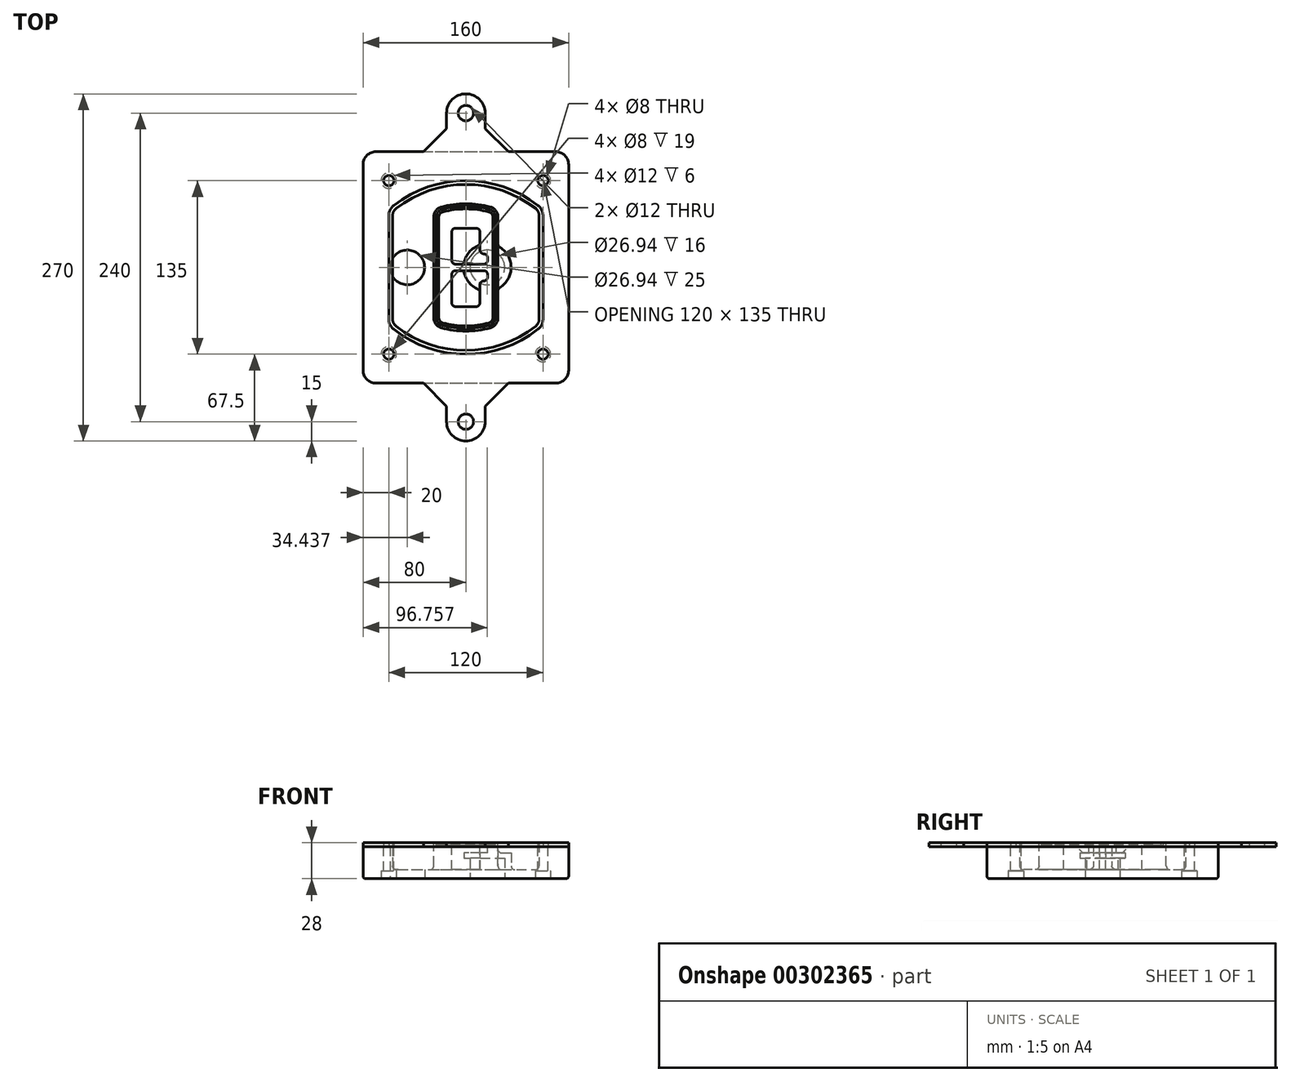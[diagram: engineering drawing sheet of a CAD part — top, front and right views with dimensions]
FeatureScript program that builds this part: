
annotation { "Feature Type Name" : "Feature", "Feature Type Description" : "" }
export const myFeature = defineFeature(function(context is Context, id is Id, definition is map)
    precondition{}
    {
        {
            var Q0;
            Q0=qCreatedBy(makeId("Top.planeOp"),FACE);
            var sketch = newSketch(context, id + "F0", { "sketchPlane" : qUnion([Q0])});
            skPoint(sketch, "E0.rect.middle", {"position": v(0, 0) * mm});
            skLineSegment(sketch, "E1.bottom", {"start": v(-70, -90) * mm, "end": v(70, -90) * mm});
            skLineSegment(sketch, "E1.top", {"start": v(-70, 90) * mm, "end": v(70, 90) * mm});
            skLineSegment(sketch, "E1.left", {"start": v(-80, -80) * mm, "end": v(-80, 80) * mm});
            skLineSegment(sketch, "E1.right", {"start": v(80, -80) * mm, "end": v(80, 80) * mm});
            skLineSegment(sketch, "E2", {"start": v(-80, 90) * mm, "end": v(80, -90) * mm, "construction": true});
            skLineSegment(sketch, "E3", {"start": v(80, 90) * mm, "end": v(-80, -90) * mm, "construction": true});
            skCircle(sketch, "E4", {"center": v(-60, 67.5) * mm, "radius": 4 * mm});
            skCircle(sketch, "E5", {"center": v(60, 67.5) * mm, "radius": 4 * mm});
            skCircle(sketch, "E6", {"center": v(60, -67.5) * mm, "radius": 4 * mm});
            skCircle(sketch, "E7", {"center": v(-60, -67.5) * mm, "radius": 4 * mm});
            skLineSegment(sketch, "E8", {"start": v(-60, 67.5) * mm, "end": v(60, 67.5) * mm, "construction": true});
            skLineSegment(sketch, "E9", {"start": v(60, 67.5) * mm, "end": v(60, -67.5) * mm, "construction": true});
            skLineSegment(sketch, "E10", {"start": v(60, -67.5) * mm, "end": v(-60, -67.5) * mm, "construction": true});
            skLineSegment(sketch, "E11", {"start": v(-60, -67.5) * mm, "end": v(-60, 67.5) * mm, "construction": true});
            skLineSegment(sketch, "E12", {"start": v(-60, 40.3) * mm, "end": v(-60, -40.3) * mm});
            skLineSegment(sketch, "E13", {"start": v(60, 40.3) * mm, "end": v(60, -40.3) * mm});
            skArc(sketch, "E14", {"start": v(56.15, 48.18) * mm, "mid": v(0, 67.5) * mm, "end": v(-56.15, 48.18) * mm});
            skArc(sketch, "E15", {"start": v(-56.15, -48.18) * mm, "mid": v(0, -67.5) * mm, "end": v(56.15, -48.18) * mm});
            skLineSegment(sketch, "E16", {"start": v(-60, 0) * mm, "end": v(60, 0) * mm, "construction": true});
            skPoint(sketch, "E17.visualSharp", {"position": v(-60, -45) * mm});
            skArc(sketch, "E17.filletArc", {"start": v(-60, -40.3) * mm, "mid": v(-58.99, -44.68) * mm, "end": v(-56.15, -48.18) * mm});
            skPoint(sketch, "E18.visualSharp", {"position": v(-60, 45) * mm});
            skArc(sketch, "E18.filletArc", {"start": v(-56.15, 48.18) * mm, "mid": v(-58.99, 44.68) * mm, "end": v(-60, 40.3) * mm});
            skPoint(sketch, "E19.visualSharp", {"position": v(60, 45) * mm});
            skArc(sketch, "E19.filletArc", {"start": v(60, 40.3) * mm, "mid": v(58.99, 44.68) * mm, "end": v(56.15, 48.18) * mm});
            skPoint(sketch, "E20.visualSharp", {"position": v(60, -45) * mm});
            skArc(sketch, "E20.filletArc", {"start": v(56.15, -48.18) * mm, "mid": v(58.99, -44.68) * mm, "end": v(60, -40.3) * mm});
            skPoint(sketch, "E21.visualSharp", {"position": v(-80, 90) * mm});
            skArc(sketch, "E21.filletArc", {"start": v(-70, 90) * mm, "mid": v(-77.07, 87.07) * mm, "end": v(-80, 80) * mm});
            skPoint(sketch, "E22.visualSharp", {"position": v(80, 90) * mm});
            skArc(sketch, "E22.filletArc", {"start": v(80, 80) * mm, "mid": v(77.07, 87.07) * mm, "end": v(70, 90) * mm});
            skPoint(sketch, "E23.visualSharp", {"position": v(80, -90) * mm});
            skArc(sketch, "E23.filletArc", {"start": v(70, -90) * mm, "mid": v(77.07, -87.07) * mm, "end": v(80, -80) * mm});
            skPoint(sketch, "E24.visualSharp", {"position": v(-80, -90) * mm});
            skArc(sketch, "E24.filletArc", {"start": v(-80, -80) * mm, "mid": v(-77.07, -87.07) * mm, "end": v(-70, -90) * mm});
            skArc(sketch, "E25.0", {"start": v(57, 40.3) * mm, "mid": v(56.3, 43.36) * mm, "end": v(54.3, 45.81) * mm});
            skLineSegment(sketch, "E25.1", {"start": v(57, 40.3) * mm, "end": v(57, -40.3) * mm});
            skArc(sketch, "E25.2", {"start": v(54.3, -45.81) * mm, "mid": v(56.3, -43.36) * mm, "end": v(57, -40.3) * mm});
            skArc(sketch, "E25.3", {"start": v(-54.3, -45.81) * mm, "mid": v(0, -64.5) * mm, "end": v(54.3, -45.81) * mm});
            skArc(sketch, "E25.4", {"start": v(-57, -40.3) * mm, "mid": v(-56.3, -43.36) * mm, "end": v(-54.3, -45.81) * mm});
            skArc(sketch, "E25.5", {"start": v(54.3, 45.81) * mm, "mid": v(0, 64.5) * mm, "end": v(-54.3, 45.81) * mm});
            skLineSegment(sketch, "E25.6", {"start": v(-57, 40.3) * mm, "end": v(-57, -40.3) * mm});
            skArc(sketch, "E25.7", {"start": v(-54.3, 45.81) * mm, "mid": v(-56.3, 43.36) * mm, "end": v(-57, 40.3) * mm});
            skArc(sketch, "E26.0", {"start": v(-58.62, 51.33) * mm, "mid": v(-62.58, 46.43) * mm, "end": v(-64, 40.3) * mm});
            skArc(sketch, "E26.1", {"start": v(58.62, 51.33) * mm, "mid": v(0, 71.5) * mm, "end": v(-58.62, 51.33) * mm});
            skArc(sketch, "E26.2", {"start": v(64, 40.3) * mm, "mid": v(62.58, 46.43) * mm, "end": v(58.62, 51.33) * mm});
            skLineSegment(sketch, "E26.3", {"start": v(64, 40.3) * mm, "end": v(64, -40.3) * mm});
            skArc(sketch, "E26.4", {"start": v(58.62, -51.33) * mm, "mid": v(62.58, -46.43) * mm, "end": v(64, -40.3) * mm});
            skLineSegment(sketch, "E26.5", {"start": v(-64, 40.3) * mm, "end": v(-64, -40.3) * mm});
            skArc(sketch, "E26.6", {"start": v(-58.62, -51.33) * mm, "mid": v(0, -71.5) * mm, "end": v(58.62, -51.33) * mm});
            skArc(sketch, "E26.7", {"start": v(-64, -40.3) * mm, "mid": v(-62.58, -46.43) * mm, "end": v(-58.62, -51.33) * mm});
            skSolve(sketch);
        }
        {
            var Q0;
            Q0=makeQuery(id+"F0.imprint","IMPRINT",FACE,{"disambiguationData":[TD([[makeQuery(id+"F0.imprint","IMPRINT",EDGE,{"derivedFrom":sQuery(id+"F0.wireOp",EDGE,"E1.bottom")}),1.0]])]});
            var Q1;
            Q1=makeQuery(id+"F0.imprint","IMPRINT",FACE,{"disambiguationData":[TD([[makeQuery(id+"F0.imprint","IMPRINT",EDGE,{"derivedFrom":sQuery(id+"F0.wireOp",EDGE,"E12")}),1.0]])]});
            var Q2;
            Q2=makeQuery(id+"F0.imprint","IMPRINT",FACE,{"disambiguationData":[TD([[makeQuery(id+"F0.imprint","IMPRINT",EDGE,{"derivedFrom":sQuery(id+"F0.wireOp",EDGE,"E25.0")}),1.0]])]});
            var Q3;
            Q3=makeQuery(id+"F0.imprint","IMPRINT",FACE,{"disambiguationData":[TD([[makeQuery(id+"F0.imprint","IMPRINT",EDGE,{"derivedFrom":sQuery(id+"F0.wireOp",EDGE,"E12")}),-1.0]])]});
            extrude(context, id + "F1", {"entities" : qUnion([Q0, Q1, Q2, Q3]), "oppositeDirection" : true, "depth" : 25 * mm});
        }
        {
            var Q0;
            Q0=makeQuery(id+"F0.imprint","IMPRINT",FACE,{"disambiguationData":[TD([[makeQuery(id+"F0.imprint","IMPRINT",EDGE,{"derivedFrom":sQuery(id+"F0.wireOp",EDGE,"E12")}),1.0]])]});
            extrude(context, id + "F2", {"entities" : qUnion([Q0]), "operationType" : NewBodyOperationType.ADD, "depth" : 3 * mm});
        }
        {
            var Q0;
            Q0=makeQuery(id+"F0.imprint","IMPRINT",FACE,{"disambiguationData":[TD([[makeQuery(id+"F0.imprint","IMPRINT",EDGE,{"derivedFrom":sQuery(id+"F0.wireOp",EDGE,"E25.0")}),1.0]])]});
            extrude(context, id + "F3", {"entities" : qUnion([Q0]), "operationType" : NewBodyOperationType.REMOVE, "oppositeDirection" : true, "depth" : 18 * mm});
        }
        {
            var Q0;
            Q0=makeQuery(id+"F2.opExtrude","CAP_FACE",FACE,{"disambiguationData":[OSD([sQuery(id+"F0.wireOp",EDGE,"E12"),sQuery(id+"F0.wireOp",EDGE,"E13"),sQuery(id+"F0.wireOp",EDGE,"E14"),sQuery(id+"F0.wireOp",EDGE,"E15"),sQuery(id+"F0.wireOp",EDGE,"E17.filletArc"),sQuery(id+"F0.wireOp",EDGE,"E18.filletArc"),sQuery(id+"F0.wireOp",EDGE,"E19.filletArc"),sQuery(id+"F0.wireOp",EDGE,"E20.filletArc"),sQuery(id+"F0.wireOp",EDGE,"E25.0"),sQuery(id+"F0.wireOp",EDGE,"E25.1"),sQuery(id+"F0.wireOp",EDGE,"E25.2"),sQuery(id+"F0.wireOp",EDGE,"E25.3"),sQuery(id+"F0.wireOp",EDGE,"E25.4"),sQuery(id+"F0.wireOp",EDGE,"E25.5"),sQuery(id+"F0.wireOp",EDGE,"E25.6"),sQuery(id+"F0.wireOp",EDGE,"E25.7")])],"isStart":false});
            var sketch = newSketch(context, id + "F4", { "sketchPlane" : qUnion([Q0])});
            skArc(sketch, "E27.0", {"start": v(-19.08, -46.97) * mm, "mid": v(0, -49.5) * mm, "end": v(19.08, -46.97) * mm});
            skArc(sketch, "E28.0", {"start": v(19.08, 46.97) * mm, "mid": v(0, 49.5) * mm, "end": v(-19.08, 46.97) * mm});
            skLineSegment(sketch, "E29", {"start": v(-25, 39.25) * mm, "end": v(-25, -39.25) * mm});
            skLineSegment(sketch, "E30", {"start": v(25, 39.25) * mm, "end": v(25, -39.25) * mm});
            skLineSegment(sketch, "E31", {"start": v(-25, 45.1) * mm, "end": v(25, 45.1) * mm, "construction": true});
            skLineSegment(sketch, "E32", {"start": v(-25, -45.1) * mm, "end": v(25, -45.1) * mm, "construction": true});
            skPoint(sketch, "E33.visualSharp", {"position": v(-25, 45.1) * mm});
            skArc(sketch, "E33.filletArc", {"start": v(-19.08, 46.97) * mm, "mid": v(-23.35, 44.11) * mm, "end": v(-25, 39.25) * mm});
            skPoint(sketch, "E34.visualSharp", {"position": v(25, 45.1) * mm});
            skArc(sketch, "E34.filletArc", {"start": v(25, 39.25) * mm, "mid": v(23.35, 44.11) * mm, "end": v(19.08, 46.97) * mm});
            skPoint(sketch, "E35.visualSharp", {"position": v(25, -45.1) * mm});
            skArc(sketch, "E35.filletArc", {"start": v(19.08, -46.97) * mm, "mid": v(23.35, -44.11) * mm, "end": v(25, -39.25) * mm});
            skPoint(sketch, "E36.visualSharp", {"position": v(-25, -45.1) * mm});
            skArc(sketch, "E36.filletArc", {"start": v(-25, -39.25) * mm, "mid": v(-23.35, -44.11) * mm, "end": v(-19.08, -46.97) * mm});
            skArc(sketch, "E37.0", {"start": v(54.3, 45.81) * mm, "mid": v(0, 64.5) * mm, "end": v(-54.3, 45.81) * mm});
            skArc(sketch, "E37.1", {"start": v(-54.3, 45.81) * mm, "mid": v(-56.3, 43.36) * mm, "end": v(-57, 40.3) * mm});
            skLineSegment(sketch, "E37.2", {"start": v(-57, 40.3) * mm, "end": v(-57, -40.3) * mm});
            skArc(sketch, "E37.3", {"start": v(-57, -40.3) * mm, "mid": v(-56.3, -43.36) * mm, "end": v(-54.3, -45.81) * mm});
            skArc(sketch, "E37.4", {"start": v(-54.3, -45.81) * mm, "mid": v(0, -64.5) * mm, "end": v(54.3, -45.81) * mm});
            skArc(sketch, "E37.5", {"start": v(54.3, -45.81) * mm, "mid": v(56.3, -43.36) * mm, "end": v(57, -40.3) * mm});
            skLineSegment(sketch, "E37.6", {"start": v(57, 40.3) * mm, "end": v(57, -40.3) * mm});
            skArc(sketch, "E37.7", {"start": v(57, 40.3) * mm, "mid": v(56.3, 43.36) * mm, "end": v(54.3, 45.81) * mm});
            skLineSegment(sketch, "E38.0", {"start": v(23, 39.25) * mm, "end": v(23, -39.25) * mm});
            skArc(sketch, "E38.1", {"start": v(18.56, -45.04) * mm, "mid": v(21.76, -42.9) * mm, "end": v(23, -39.25) * mm});
            skArc(sketch, "E38.2", {"start": v(-18.56, -45.04) * mm, "mid": v(0, -47.5) * mm, "end": v(18.56, -45.04) * mm});
            skArc(sketch, "E38.3", {"start": v(-23, -39.25) * mm, "mid": v(-21.76, -42.9) * mm, "end": v(-18.56, -45.04) * mm});
            skLineSegment(sketch, "E38.4", {"start": v(-23, 39.25) * mm, "end": v(-23, -39.25) * mm});
            skArc(sketch, "E38.5", {"start": v(23, 39.25) * mm, "mid": v(21.76, 42.9) * mm, "end": v(18.56, 45.04) * mm});
            skArc(sketch, "E38.6", {"start": v(-18.56, 45.04) * mm, "mid": v(-21.76, 42.9) * mm, "end": v(-23, 39.25) * mm});
            skArc(sketch, "E38.7", {"start": v(18.56, 45.04) * mm, "mid": v(0, 47.5) * mm, "end": v(-18.56, 45.04) * mm});
            skArc(sketch, "E39.0", {"start": v(21, 39.25) * mm, "mid": v(20.18, 41.68) * mm, "end": v(18.04, 43.1) * mm});
            skLineSegment(sketch, "E39.1", {"start": v(21, 39.25) * mm, "end": v(21, -39.25) * mm});
            skArc(sketch, "E39.2", {"start": v(18.04, -43.1) * mm, "mid": v(20.18, -41.68) * mm, "end": v(21, -39.25) * mm});
            skArc(sketch, "E39.3", {"start": v(-18.04, -43.1) * mm, "mid": v(0, -45.5) * mm, "end": v(18.04, -43.1) * mm});
            skArc(sketch, "E39.4", {"start": v(-21, -39.25) * mm, "mid": v(-20.18, -41.68) * mm, "end": v(-18.04, -43.1) * mm});
            skArc(sketch, "E39.5", {"start": v(18.04, 43.1) * mm, "mid": v(0, 45.5) * mm, "end": v(-18.04, 43.1) * mm});
            skLineSegment(sketch, "E39.6", {"start": v(-21, 39.25) * mm, "end": v(-21, -39.25) * mm});
            skArc(sketch, "E39.7", {"start": v(-18.04, 43.1) * mm, "mid": v(-20.18, 41.68) * mm, "end": v(-21, 39.25) * mm});
            skLineSegment(sketch, "E40", {"start": v(-25, 0) * mm, "end": v(25, 0) * mm, "construction": true});
            skLineSegment(sketch, "E41", {"start": v(-11, 5.5) * mm, "end": v(-11, 27.5) * mm});
            skLineSegment(sketch, "E42", {"start": v(-8, 30.5) * mm, "end": v(8, 30.5) * mm});
            skLineSegment(sketch, "E43", {"start": v(11, 27.5) * mm, "end": v(11, 13.5) * mm});
            skLineSegment(sketch, "E44", {"start": v(14, 10.5) * mm, "end": v(14, 10.5) * mm});
            skLineSegment(sketch, "E45", {"start": v(17, 7.5) * mm, "end": v(17, 5.5) * mm});
            skLineSegment(sketch, "E46", {"start": v(14, 2.5) * mm, "end": v(-8, 2.5) * mm});
            skPoint(sketch, "E47.visualSharp", {"position": v(-11, 30.5) * mm});
            skArc(sketch, "E47.filletArc", {"start": v(-8, 30.5) * mm, "mid": v(-10.12, 29.62) * mm, "end": v(-11, 27.5) * mm});
            skPoint(sketch, "E48.visualSharp", {"position": v(11, 30.5) * mm});
            skArc(sketch, "E48.filletArc", {"start": v(11, 27.5) * mm, "mid": v(10.12, 29.62) * mm, "end": v(8, 30.5) * mm});
            skPoint(sketch, "E49.visualSharp", {"position": v(11, 10.5) * mm});
            skArc(sketch, "E49.filletArc", {"start": v(11, 13.5) * mm, "mid": v(11.88, 11.38) * mm, "end": v(14, 10.5) * mm});
            skPoint(sketch, "E50.visualSharp", {"position": v(17, 10.5) * mm});
            skArc(sketch, "E50.filletArc", {"start": v(17, 7.5) * mm, "mid": v(16.12, 9.62) * mm, "end": v(14, 10.5) * mm});
            skPoint(sketch, "E51.visualSharp", {"position": v(17, 2.5) * mm});
            skArc(sketch, "E51.filletArc", {"start": v(14, 2.5) * mm, "mid": v(16.12, 3.38) * mm, "end": v(17, 5.5) * mm});
            skPoint(sketch, "E52.visualSharp", {"position": v(-11, 2.5) * mm});
            skArc(sketch, "E52.filletArc", {"start": v(-11, 5.5) * mm, "mid": v(-10.12, 3.38) * mm, "end": v(-8, 2.5) * mm});
            skLineSegment(sketch, "E53.0.MirrorCS", {"start": v(14, -2.5) * mm, "end": v(-8, -2.5) * mm});
            skArc(sketch, "E54.0.MirrorCS", {"start": v(-11, -5.5) * mm, "mid": v(-10.12, -3.38) * mm, "end": v(-8, -2.5) * mm});
            skLineSegment(sketch, "E55.0.MirrorCS", {"start": v(-11, -5.5) * mm, "end": v(-11, -27.5) * mm});
            skArc(sketch, "E56.0.MirrorCS", {"start": v(-8, -30.5) * mm, "mid": v(-10.12, -29.62) * mm, "end": v(-11, -27.5) * mm});
            skLineSegment(sketch, "E57.0.MirrorCS", {"start": v(-8, -30.5) * mm, "end": v(8, -30.5) * mm});
            skArc(sketch, "E58.0.MirrorCS", {"start": v(11, -27.5) * mm, "mid": v(10.12, -29.62) * mm, "end": v(8, -30.5) * mm});
            skLineSegment(sketch, "E59.0.MirrorCS", {"start": v(11, -27.5) * mm, "end": v(11, -13.5) * mm});
            skArc(sketch, "E60.0.MirrorCS", {"start": v(11, -13.5) * mm, "mid": v(11.88, -11.38) * mm, "end": v(14, -10.5) * mm});
            skArc(sketch, "E61.0.MirrorCS", {"start": v(17, -7.5) * mm, "mid": v(16.12, -9.62) * mm, "end": v(14, -10.5) * mm});
            skLineSegment(sketch, "E62.0.MirrorCS", {"start": v(17, -7.5) * mm, "end": v(17, -5.5) * mm});
            skArc(sketch, "E63.0.MirrorCS", {"start": v(14, -2.5) * mm, "mid": v(16.12, -3.38) * mm, "end": v(17, -5.5) * mm});
            skSolve(sketch);
        }
        {
            var Q0;
            Q0=makeQuery(id+"F4.imprint","IMPRINT",FACE,{"disambiguationData":[TD([[makeQuery(id+"F4.imprint","IMPRINT",EDGE,{"derivedFrom":sQuery(id+"F4.wireOp",EDGE,"E27.0")}),1.0]])]});
            var Q1;
            Q1=makeQuery(id+"F4.imprint","IMPRINT",FACE,{"disambiguationData":[TD([[makeQuery(id+"F4.imprint","IMPRINT",EDGE,{"derivedFrom":sQuery(id+"F4.wireOp",EDGE,"E38.0")}),-1.0]])]});
            var Q2;
            Q2=makeQuery(id+"F4.imprint","IMPRINT",FACE,{"disambiguationData":[TD([[makeQuery(id+"F4.imprint","IMPRINT",EDGE,{"derivedFrom":sQuery(id+"F4.wireOp",EDGE,"E39.0")}),1.0]])]});
            extrude(context, id + "F5", {"entities" : qUnion([Q0, Q1, Q2]), "operationType" : NewBodyOperationType.ADD, "endBound" : BoundingType.UP_TO_NEXT, "oppositeDirection" : true, "depth" : 25 * mm});
        }
        {
            var Q0;
            Q0=makeQuery(id+"F4.imprint","IMPRINT",FACE,{"disambiguationData":[TD([[makeQuery(id+"F4.imprint","IMPRINT",EDGE,{"derivedFrom":sQuery(id+"F4.wireOp",EDGE,"E38.0")}),-1.0]])]});
            extrude(context, id + "F6", {"entities" : qUnion([Q0]), "operationType" : NewBodyOperationType.REMOVE, "oppositeDirection" : true, "depth" : 2 * mm});
        }
        {
            var Q0;
            Q0=makeQuery(id+"F1.opExtrude","CAP_FACE",FACE,{"disambiguationData":[OSD([sQuery(id+"F0.wireOp",EDGE,"E1.bottom"),sQuery(id+"F0.wireOp",EDGE,"E1.top"),sQuery(id+"F0.wireOp",EDGE,"E1.left"),sQuery(id+"F0.wireOp",EDGE,"E1.right"),sQuery(id+"F0.wireOp",EDGE,"E4"),sQuery(id+"F0.wireOp",EDGE,"E5"),sQuery(id+"F0.wireOp",EDGE,"E6"),sQuery(id+"F0.wireOp",EDGE,"E7"),sQuery(id+"F0.wireOp",EDGE,"E21.filletArc"),sQuery(id+"F0.wireOp",EDGE,"E22.filletArc"),sQuery(id+"F0.wireOp",EDGE,"E23.filletArc"),sQuery(id+"F0.wireOp",EDGE,"E24.filletArc")])],"isStart":false});
            var sketch = newSketch(context, id + "F7", { "sketchPlane" : qUnion([Q0])});
            skCircle(sketch, "E64", {"center": v(16.76, 0) * mm, "radius": 13.47 * mm});
            skCircle(sketch, "E65", {"center": v(-45.56, 0) * mm, "radius": 13.47 * mm});
            skLineSegment(sketch, "E66", {"start": v(80, 0) * mm, "end": v(-80, 0) * mm});
            skCircle(sketch, "E67", {"center": v(16.76, 0) * mm, "radius": 18.47 * mm});
            skCircle(sketch, "E68", {"center": v(60, -67.5) * mm, "radius": 6 * mm});
            skCircle(sketch, "E69", {"center": v(-60, -67.5) * mm, "radius": 6 * mm});
            skCircle(sketch, "E70", {"center": v(-60, 67.5) * mm, "radius": 6 * mm});
            skCircle(sketch, "E71", {"center": v(60, 67.5) * mm, "radius": 6 * mm});
            skSolve(sketch);
        }
        {
            var Q0;
            {var subQ1=sQuery(id+"F7.wireOp",EDGE,"E66");var subQ4=sQuery(id+"F7.wireOp",EDGE,"E64");var subQ6=makeQuery(id+"F7.imprint","INTERSECT",VERTEX,{"disambiguationData":[OD(0.0)],"derivedFrom":[subQ4,subQ1]});Q0=makeQuery(id+"F7.imprint","IMPRINT",FACE,{"disambiguationData":[TD([[makeQuery(id+"F7.imprint","IMPRINT",EDGE,{"disambiguationData":[TD([[subQ6,-1.0]])],"derivedFrom":subQ4}),-1.0]])]});}
            var Q1;
            {var subQ0=sQuery(id+"F7.wireOp",EDGE,"E66");var subQ1=sQuery(id+"F7.wireOp",EDGE,"E64");var subQ3=makeQuery(id+"F7.imprint","INTERSECT",VERTEX,{"disambiguationData":[OD(0.0)],"derivedFrom":[subQ1,subQ0]});Q1=makeQuery(id+"F7.imprint","IMPRINT",FACE,{"disambiguationData":[TD([[makeQuery(id+"F7.imprint","IMPRINT",EDGE,{"disambiguationData":[TD([[subQ3,-1.0]])],"derivedFrom":subQ1}),1.0]])]});}
            var Q2;
            {var subQ0=sQuery(id+"F7.wireOp",EDGE,"E66");var subQ1=sQuery(id+"F7.wireOp",EDGE,"E64");var subQ3=makeQuery(id+"F7.imprint","INTERSECT",VERTEX,{"disambiguationData":[OD(0.0)],"derivedFrom":[subQ1,subQ0]});Q2=makeQuery(id+"F7.imprint","IMPRINT",FACE,{"disambiguationData":[TD([[makeQuery(id+"F7.imprint","IMPRINT",EDGE,{"disambiguationData":[TD([[subQ3,1.0]])],"derivedFrom":subQ1}),1.0]])]});}
            var Q3;
            {var subQ1=sQuery(id+"F7.wireOp",EDGE,"E66");var subQ4=sQuery(id+"F7.wireOp",EDGE,"E64");var subQ6=makeQuery(id+"F7.imprint","INTERSECT",VERTEX,{"disambiguationData":[OD(0.0)],"derivedFrom":[subQ4,subQ1]});Q3=makeQuery(id+"F7.imprint","IMPRINT",FACE,{"disambiguationData":[TD([[makeQuery(id+"F7.imprint","IMPRINT",EDGE,{"disambiguationData":[TD([[subQ6,1.0]])],"derivedFrom":subQ4}),-1.0]])]});}
            extrude(context, id + "F8", {"entities" : qUnion([Q0, Q1, Q2, Q3]), "operationType" : NewBodyOperationType.ADD, "oppositeDirection" : true, "depth" : 20 * mm});
        }
        {
            var Q0;
            {var subQ0=sQuery(id+"F7.wireOp",EDGE,"E66");var subQ1=sQuery(id+"F7.wireOp",EDGE,"E64");var subQ3=makeQuery(id+"F7.imprint","INTERSECT",VERTEX,{"disambiguationData":[OD(0.0)],"derivedFrom":[subQ1,subQ0]});Q0=makeQuery(id+"F7.imprint","IMPRINT",FACE,{"disambiguationData":[TD([[makeQuery(id+"F7.imprint","IMPRINT",EDGE,{"disambiguationData":[TD([[subQ3,-1.0]])],"derivedFrom":subQ1}),1.0]])]});}
            var Q1;
            {var subQ0=sQuery(id+"F7.wireOp",EDGE,"E66");var subQ1=sQuery(id+"F7.wireOp",EDGE,"E64");var subQ3=makeQuery(id+"F7.imprint","INTERSECT",VERTEX,{"disambiguationData":[OD(0.0)],"derivedFrom":[subQ1,subQ0]});Q1=makeQuery(id+"F7.imprint","IMPRINT",FACE,{"disambiguationData":[TD([[makeQuery(id+"F7.imprint","IMPRINT",EDGE,{"disambiguationData":[TD([[subQ3,1.0]])],"derivedFrom":subQ1}),1.0]])]});}
            extrude(context, id + "F9", {"entities" : qUnion([Q0, Q1]), "operationType" : NewBodyOperationType.REMOVE, "oppositeDirection" : true, "depth" : 16 * mm});
        }
        {
            var Q0;
            {var subQ0=sQuery(id+"F7.wireOp",EDGE,"E66");var subQ1=sQuery(id+"F7.wireOp",EDGE,"E65");var subQ3=makeQuery(id+"F7.imprint","INTERSECT",VERTEX,{"disambiguationData":[OD(0.0)],"derivedFrom":[subQ1,subQ0]});Q0=makeQuery(id+"F7.imprint","IMPRINT",FACE,{"disambiguationData":[TD([[makeQuery(id+"F7.imprint","IMPRINT",EDGE,{"disambiguationData":[TD([[subQ3,-1.0]])],"derivedFrom":subQ1}),1.0]])]});}
            var Q1;
            {var subQ0=sQuery(id+"F7.wireOp",EDGE,"E66");var subQ1=sQuery(id+"F7.wireOp",EDGE,"E65");var subQ3=makeQuery(id+"F7.imprint","INTERSECT",VERTEX,{"disambiguationData":[OD(0.0)],"derivedFrom":[subQ1,subQ0]});Q1=makeQuery(id+"F7.imprint","IMPRINT",FACE,{"disambiguationData":[TD([[makeQuery(id+"F7.imprint","IMPRINT",EDGE,{"disambiguationData":[TD([[subQ3,1.0]])],"derivedFrom":subQ1}),1.0]])]});}
            extrude(context, id + "F10", {"entities" : qUnion([Q0, Q1]), "operationType" : NewBodyOperationType.REMOVE, "oppositeDirection" : true, "depth" : 25 * mm});
        }
        {
            var Q0;
            Q0=makeQuery(id+"F7.imprint","IMPRINT",FACE,{"disambiguationData":[TD([[makeQuery(id+"F7.imprint","IMPRINT",EDGE,{"derivedFrom":sQuery(id+"F7.wireOp",EDGE,"E68")}),1.0]])]});
            var Q1;
            Q1=makeQuery(id+"F7.imprint","IMPRINT",FACE,{"disambiguationData":[TD([[makeQuery(id+"F7.imprint","IMPRINT",EDGE,{"derivedFrom":makeQuery(id+"F1.opExtrude","CAP_EDGE",EDGE,{"disambiguationData":[OSD([sQuery(id+"F0.wireOp",EDGE,"E5")])],"isStart":false})}),-1.0]])]});
            var Q2;
            Q2=makeQuery(id+"F7.imprint","IMPRINT",FACE,{"disambiguationData":[TD([[makeQuery(id+"F7.imprint","IMPRINT",EDGE,{"derivedFrom":sQuery(id+"F7.wireOp",EDGE,"E69")}),1.0]])]});
            var Q3;
            Q3=makeQuery(id+"F7.imprint","IMPRINT",FACE,{"disambiguationData":[TD([[makeQuery(id+"F7.imprint","IMPRINT",EDGE,{"derivedFrom":makeQuery(id+"F1.opExtrude","CAP_EDGE",EDGE,{"disambiguationData":[OSD([sQuery(id+"F0.wireOp",EDGE,"E4")])],"isStart":false})}),-1.0]])]});
            var Q4;
            Q4=makeQuery(id+"F7.imprint","IMPRINT",FACE,{"disambiguationData":[TD([[makeQuery(id+"F7.imprint","IMPRINT",EDGE,{"derivedFrom":sQuery(id+"F7.wireOp",EDGE,"E70")}),1.0]])]});
            var Q5;
            Q5=makeQuery(id+"F7.imprint","IMPRINT",FACE,{"disambiguationData":[TD([[makeQuery(id+"F7.imprint","IMPRINT",EDGE,{"derivedFrom":makeQuery(id+"F1.opExtrude","CAP_EDGE",EDGE,{"disambiguationData":[OSD([sQuery(id+"F0.wireOp",EDGE,"E7")])],"isStart":false})}),-1.0]])]});
            var Q6;
            Q6=makeQuery(id+"F7.imprint","IMPRINT",FACE,{"disambiguationData":[TD([[makeQuery(id+"F7.imprint","IMPRINT",EDGE,{"derivedFrom":sQuery(id+"F7.wireOp",EDGE,"E71")}),1.0]])]});
            var Q7;
            Q7=makeQuery(id+"F7.imprint","IMPRINT",FACE,{"disambiguationData":[TD([[makeQuery(id+"F7.imprint","IMPRINT",EDGE,{"derivedFrom":makeQuery(id+"F1.opExtrude","CAP_EDGE",EDGE,{"disambiguationData":[OSD([sQuery(id+"F0.wireOp",EDGE,"E6")])],"isStart":false})}),-1.0]])]});
            extrude(context, id + "F11", {"entities" : qUnion([Q0, Q1, Q2, Q3, Q4, Q5, Q6, Q7]), "operationType" : NewBodyOperationType.REMOVE, "oppositeDirection" : true, "depth" : 6 * mm});
        }
        {
            var Q0;
            Q0=makeQuery(id+"F9.boolean.opBoolean","COPY",FACE,{"derivedFrom":makeQuery(id+"F9.opExtrude","CAP_FACE",FACE,{"disambiguationData":[OSD([sQuery(id+"F7.wireOp",EDGE,"E64")])],"isStart":false})});
            var sketch = newSketch(context, id + "F12", { "sketchPlane" : qUnion([Q0])});
            skArc(sketch, "E72.0", {"start": v(11, 17.55) * mm, "mid": v(2.57, 11.82) * mm, "end": v(-1.54, 2.5) * mm});
            skArc(sketch, "E72.1", {"start": v(-1.54, -2.5) * mm, "mid": v(2.57, -11.82) * mm, "end": v(11, -17.55) * mm});
            skLineSegment(sketch, "E73", {"start": v(-1.54, -2.5) * mm, "end": v(14, -2.5) * mm});
            skLineSegment(sketch, "E74.0", {"start": v(14, 2.5) * mm, "end": v(-1.54, 2.5) * mm});
            skArc(sketch, "E74.1", {"start": v(14, 2.5) * mm, "mid": v(16.12, 3.38) * mm, "end": v(17, 5.5) * mm});
            skLineSegment(sketch, "E74.2", {"start": v(17, 7.5) * mm, "end": v(17, 5.5) * mm});
            skArc(sketch, "E74.3", {"start": v(17, 7.5) * mm, "mid": v(16.12, 9.62) * mm, "end": v(14, 10.5) * mm});
            skArc(sketch, "E74.4", {"start": v(11, 13.5) * mm, "mid": v(11.88, 11.38) * mm, "end": v(14, 10.5) * mm});
            skLineSegment(sketch, "E74.5", {"start": v(11, 17.55) * mm, "end": v(11, 13.5) * mm});
            skLineSegment(sketch, "E74.7", {"start": v(14, -2.5) * mm, "end": v(-1.54, -2.5) * mm});
            skArc(sketch, "E74.8", {"start": v(14, -2.5) * mm, "mid": v(16.12, -3.38) * mm, "end": v(17, -5.5) * mm});
            skLineSegment(sketch, "E74.9", {"start": v(17, -7.5) * mm, "end": v(17, -5.5) * mm});
            skArc(sketch, "E74.10", {"start": v(17, -7.5) * mm, "mid": v(16.12, -9.62) * mm, "end": v(14, -10.5) * mm});
            skArc(sketch, "E74.11", {"start": v(11, -13.5) * mm, "mid": v(11.88, -11.38) * mm, "end": v(14, -10.5) * mm});
            skLineSegment(sketch, "E74.12", {"start": v(11, -17.55) * mm, "end": v(11, -13.5) * mm});
            skPoint(sketch, "E75.orphan", {"position": v(11, -27.5) * mm});
            skPoint(sketch, "E76.orphan", {"position": v(-8, -2.5) * mm});
            skPoint(sketch, "E77.orphan", {"position": v(-8, 2.5) * mm});
            skPoint(sketch, "E78.orphan", {"position": v(11, 27.5) * mm});
            skSolve(sketch);
        }
        {
            var Q0;
            {var subQ7=sQuery(id+"F12.wireOp",EDGE,"E72.0");var subQ14=sQuery(id+"F12.wireOp",EDGE,"E72.1");var subQ16=sQuery(id+"F12.wireOp",EDGE,"E74.1");var subQ18=sQuery(id+"F12.wireOp",EDGE,"E74.8");Q0=qUnion([makeQuery(id+"F12.imprint","IMPRINT",FACE,{"disambiguationData":[TD([[makeQuery(id+"F12.imprint","IMPRINT",EDGE,{"derivedFrom":subQ7}),1.0]])]}),makeQuery(id+"F12.imprint","IMPRINT",FACE,{"disambiguationData":[TD([[makeQuery(id+"F12.imprint","IMPRINT",EDGE,{"derivedFrom":subQ14}),1.0]])]}),makeQuery(id+"F12.imprint","IMPRINT",FACE,{"disambiguationData":[TD([[makeQuery(id+"F12.imprint","IMPRINT",EDGE,{"derivedFrom":subQ16}),1.0]])]}),makeQuery(id+"F12.imprint","IMPRINT",FACE,{"disambiguationData":[TD([[makeQuery(id+"F12.imprint","IMPRINT",EDGE,{"derivedFrom":subQ18}),-1.0]])]})]);}
            var Q1;
            Q1=makeQuery(id+"F5.boolean.opBoolean","SPLIT",FACE,{"disambiguationData":[TD([makeQuery(id+"F5.opExtrude","SWEPT_FACE",FACE,{"disambiguationData":[OSD([sQuery(id+"F4.wireOp",EDGE,"E41")])]})])],"derivedFrom":makeQuery(id+"F3.boolean.opBoolean","COPY",FACE,{"derivedFrom":makeQuery(id+"F3.opExtrude","CAP_FACE",FACE,{"disambiguationData":[OSD([sQuery(id+"F0.wireOp",EDGE,"E25.0"),sQuery(id+"F0.wireOp",EDGE,"E25.1"),sQuery(id+"F0.wireOp",EDGE,"E25.2"),sQuery(id+"F0.wireOp",EDGE,"E25.3"),sQuery(id+"F0.wireOp",EDGE,"E25.4"),sQuery(id+"F0.wireOp",EDGE,"E25.5"),sQuery(id+"F0.wireOp",EDGE,"E25.6"),sQuery(id+"F0.wireOp",EDGE,"E25.7")])],"isStart":false})})});
            extrude(context, id + "F13", {"entities" : qUnion([Q0]), "operationType" : NewBodyOperationType.REMOVE, "endBound" : BoundingType.UP_TO_SURFACE, "endBoundEntityFace" : qUnion([Q1]), "depth" : 25 * mm});
        }
        {
            var Q0;
            Q0=makeQuery(id+"F3.boolean.opBoolean","COPY",EDGE,{"derivedFrom":makeQuery(id+"F3.opExtrude","CAP_EDGE",EDGE,{"disambiguationData":[OSD([sQuery(id+"F0.wireOp",EDGE,"E25.6")])],"isStart":false})});
            var Q1;
            Q1=makeQuery(id+"F8.boolean.opBoolean","INTERSECT",EDGE,{"derivedFrom":[makeQuery(id+"F5.opExtrude","SWEPT_FACE",FACE,{"disambiguationData":[OSD([sQuery(id+"F4.wireOp",EDGE,"E30")])]}),makeQuery(id+"F8.opExtrude","CAP_FACE",FACE,{"disambiguationData":[OSD([sQuery(id+"F7.wireOp",EDGE,"E67")])],"isStart":false})]});
            var Q2;
            Q2=makeQuery(id+"F8.boolean.opBoolean","INTERSECT",EDGE,{"disambiguationData":[OD(1.0)],"derivedFrom":[makeQuery(id+"F5.opExtrude","SWEPT_FACE",FACE,{"disambiguationData":[OSD([sQuery(id+"F4.wireOp",EDGE,"E30")])]}),makeQuery(id+"F8.opExtrude","SWEPT_FACE",FACE,{"disambiguationData":[OSD([sQuery(id+"F7.wireOp",EDGE,"E67")])]})]});
            var Q3;
            {var subQ0=sQuery(id+"F4.wireOp",EDGE,"E30");Q3=makeQuery(id+"F8.boolean.opBoolean","SPLIT",EDGE,{"disambiguationData":[TD([makeQuery(id+"F5.opExtrude","SWEPT_FACE",FACE,{"disambiguationData":[OSD([sQuery(id+"F4.wireOp",EDGE,"E35.filletArc")])]})])],"derivedFrom":makeQuery(id+"F5.opExtrude","CAP_EDGE",EDGE,{"disambiguationData":[OSD([subQ0])],"isStart":false})});}
            var Q4;
            {var subQ0=sQuery(id+"F0.wireOp",EDGE,"E25.7");var subQ1=sQuery(id+"F0.wireOp",EDGE,"E25.1");var subQ2=sQuery(id+"F0.wireOp",EDGE,"E25.6");var subQ3=sQuery(id+"F0.wireOp",EDGE,"E25.5");var subQ4=sQuery(id+"F0.wireOp",EDGE,"E25.4");var subQ5=sQuery(id+"F0.wireOp",EDGE,"E25.0");var subQ6=sQuery(id+"F0.wireOp",EDGE,"E25.2");var subQ7=sQuery(id+"F0.wireOp",EDGE,"E25.3");Q4=makeQuery(id+"F8.boolean.opBoolean","INTERSECT",EDGE,{"derivedFrom":[makeQuery(id+"F5.boolean.opBoolean","SPLIT",FACE,{"disambiguationData":[TD([makeQuery(id+"F2.opExtrude","SWEPT_FACE",FACE,{"disambiguationData":[OSD([subQ5])]})])],"derivedFrom":makeQuery(id+"F3.boolean.opBoolean","COPY",FACE,{"derivedFrom":makeQuery(id+"F3.opExtrude","CAP_FACE",FACE,{"disambiguationData":[OSD([subQ5,subQ1,subQ6,subQ7,subQ4,subQ3,subQ2,subQ0])],"isStart":false})})}),makeQuery(id+"F8.opExtrude","SWEPT_FACE",FACE,{"disambiguationData":[OSD([sQuery(id+"F7.wireOp",EDGE,"E67")])]})]});}
            var Q5;
            Q5=makeQuery(id+"F8.boolean.opBoolean","INTERSECT",EDGE,{"disambiguationData":[OD(0.0)],"derivedFrom":[makeQuery(id+"F5.opExtrude","SWEPT_FACE",FACE,{"disambiguationData":[OSD([sQuery(id+"F4.wireOp",EDGE,"E30")])]}),makeQuery(id+"F8.opExtrude","SWEPT_FACE",FACE,{"disambiguationData":[OSD([sQuery(id+"F7.wireOp",EDGE,"E67")])]})]});
            fillet(context, id + "F14", {"entities" : qUnion([Q0, Q1, Q2, Q3, Q4, Q5]), "radius" : 3 * mm, "tangentPropagation" : true, "allowEdgeOverflow" : false});
        }
        {
            var Q0;
            Q0=makeQuery(id+"F1.opExtrude","CAP_EDGE",EDGE,{"disambiguationData":[OSD([sQuery(id+"F0.wireOp",EDGE,"E1.bottom")])],"isStart":false});
            fillet(context, id + "F15", {"entities" : qUnion([Q0]), "radius" : 2 * mm, "tangentPropagation" : true, "allowEdgeOverflow" : false});
        }
        {
            var Q0;
            {var subQ0=sQuery(id+"F0.wireOp",EDGE,"E21.filletArc");var subQ1=sQuery(id+"F0.wireOp",EDGE,"E7");var subQ2=sQuery(id+"F0.wireOp",EDGE,"E6");var subQ3=sQuery(id+"F0.wireOp",EDGE,"E5");var subQ4=sQuery(id+"F0.wireOp",EDGE,"E4");var subQ5=sQuery(id+"F0.wireOp",EDGE,"E22.filletArc");var subQ6=sQuery(id+"F0.wireOp",EDGE,"E1.bottom");var subQ7=sQuery(id+"F0.wireOp",EDGE,"E1.right");var subQ8=sQuery(id+"F0.wireOp",EDGE,"E1.top");var subQ9=sQuery(id+"F0.wireOp",EDGE,"E1.left");var subQ10=sQuery(id+"F0.wireOp",EDGE,"E23.filletArc");var subQ11=sQuery(id+"F0.wireOp",EDGE,"E24.filletArc");Q0=makeQuery(id+"F2.boolean.opBoolean","SPLIT",FACE,{"disambiguationData":[TD([makeQuery(id+"F1.opExtrude","SWEPT_FACE",FACE,{"disambiguationData":[OSD([subQ6])]})])],"derivedFrom":makeQuery(id+"F1.opExtrude","CAP_FACE",FACE,{"disambiguationData":[OSD([subQ6,subQ8,subQ9,subQ7,subQ4,subQ3,subQ2,subQ1,subQ0,subQ5,subQ10,subQ11])],"isStart":true})});}
            var sketch = newSketch(context, id + "F16", { "sketchPlane" : qUnion([Q0])});
            skCircle(sketch, "E79", {"center": v(0, 120) * mm, "radius": 6 * mm});
            skLineSegment(sketch, "E80", {"start": v(-33, 90) * mm, "end": v(-15, 108) * mm});
            skLineSegment(sketch, "E81", {"start": v(33, 90) * mm, "end": v(15, 108) * mm});
            skLineSegment(sketch, "E82", {"start": v(-15, 108) * mm, "end": v(-15, 120) * mm});
            skLineSegment(sketch, "E83", {"start": v(15, 108) * mm, "end": v(15, 120) * mm});
            skArc(sketch, "E84", {"start": v(15, 120) * mm, "mid": v(0, 135) * mm, "end": v(-15, 120) * mm});
            skLineSegment(sketch, "E85", {"start": v(0, 120) * mm, "end": v(0, 90) * mm, "construction": true});
            skLineSegment(sketch, "E86", {"start": v(-80, 0) * mm, "end": v(80, 0) * mm, "construction": true});
            skLineSegment(sketch, "E87.MirrorCS", {"start": v(-15, -108) * mm, "end": v(-15, -120) * mm});
            skLineSegment(sketch, "E88.MirrorCS", {"start": v(15, -108) * mm, "end": v(15, -120) * mm});
            skCircle(sketch, "E89.MirrorC", {"center": v(0, -120) * mm, "radius": 6 * mm});
            skLineSegment(sketch, "E90.MirrorCS", {"start": v(-33, -90) * mm, "end": v(-15, -108) * mm});
            skLineSegment(sketch, "E91.MirrorCS", {"start": v(33, -90) * mm, "end": v(15, -108) * mm});
            skArc(sketch, "E92.MirrorCS", {"start": v(15, -120) * mm, "mid": v(0, -135) * mm, "end": v(-15, -120) * mm});
            skLineSegment(sketch, "E93.MirrorCS", {"start": v(0, -120) * mm, "end": v(0, -90) * mm, "construction": true});
            skSolve(sketch);
        }
        {
            var Q0;
            Q0=makeQuery(id+"F16.imprint","IMPRINT",FACE,{"disambiguationData":[TD([[makeQuery(id+"F16.imprint","IMPRINT",EDGE,{"derivedFrom":sQuery(id+"F16.wireOp",EDGE,"E87.MirrorCS")}),1.0]])]});
            var Q1;
            Q1=makeQuery(id+"F16.imprint","IMPRINT",FACE,{"disambiguationData":[TD([[makeQuery(id+"F16.imprint","IMPRINT",EDGE,{"derivedFrom":sQuery(id+"F16.wireOp",EDGE,"E79")}),-1.0]])]});
            var Q2;
            Q2=makeQuery(id+"F16.imprint","IMPRINT",FACE,{"disambiguationData":[TD([[makeQuery(id+"F16.imprint","IMPRINT",EDGE,{"derivedFrom":makeQuery(id+"F1.opExtrude","CAP_EDGE",EDGE,{"disambiguationData":[OSD([sQuery(id+"F0.wireOp",EDGE,"E1.left")])],"isStart":true})}),-1.0]])]});
            var Q3;
            Q3=makeQuery(id+"F2.opExtrude","CAP_FACE",FACE,{"disambiguationData":[OSD([sQuery(id+"F0.wireOp",EDGE,"E12"),sQuery(id+"F0.wireOp",EDGE,"E13"),sQuery(id+"F0.wireOp",EDGE,"E14"),sQuery(id+"F0.wireOp",EDGE,"E15"),sQuery(id+"F0.wireOp",EDGE,"E17.filletArc"),sQuery(id+"F0.wireOp",EDGE,"E18.filletArc"),sQuery(id+"F0.wireOp",EDGE,"E19.filletArc"),sQuery(id+"F0.wireOp",EDGE,"E20.filletArc"),sQuery(id+"F0.wireOp",EDGE,"E25.0"),sQuery(id+"F0.wireOp",EDGE,"E25.1"),sQuery(id+"F0.wireOp",EDGE,"E25.2"),sQuery(id+"F0.wireOp",EDGE,"E25.3"),sQuery(id+"F0.wireOp",EDGE,"E25.4"),sQuery(id+"F0.wireOp",EDGE,"E25.5"),sQuery(id+"F0.wireOp",EDGE,"E25.6"),sQuery(id+"F0.wireOp",EDGE,"E25.7")])],"isStart":false});
            extrude(context, id + "F17", {"entities" : qUnion([Q0, Q1, Q2]), "endBound" : BoundingType.UP_TO_SURFACE, "endBoundEntityFace" : qUnion([Q3]), "depth" : 25 * mm});
        }
    });
